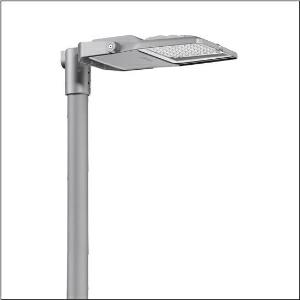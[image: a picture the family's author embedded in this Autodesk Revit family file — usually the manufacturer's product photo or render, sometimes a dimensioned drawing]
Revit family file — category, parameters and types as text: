
# Revit family: floodlight_fl_21_mini___pl33t_5xa7775d2f3a_2fb5
name_source: partatom
category: Lighting Fixtures
units: mm (PartAtom-declared; Revit-internal decimal feet)

## family parameters
Cut with Voids When Loaded = No
Host = Face
Light Source = No
Part Type = Normal
Room Calculation Point = No
Round Connector Dimension = Use Diameter
Shared = No

## types (1)
- --- (1 x LED, 17630 lm, 142.9 W, 3000K)
    Apparent Load = 143 VA
    CIE Flux Codes = 26 75 99 100 100
    Color Rendering = 70
    Color Temperature = 3000K
    Default Elevation = 1800 mm
    Description = Floodlight FL 21 mini, floodlight, primary light control with lens, of PMMA, primary optical cover: protective disc, of toughened safety glass, transparent, light distribution: PL33T, light emission: direct distribution, installation type: surface-mounted, LED, High Power LED, rated luminous flux: 17.630lm, luminous efficacy: 123lm/W, light colour: 730, colour temperature: 3000K, control: flexible luminous flux parameterisation, time-dependent luminous flux control, constant luminous flux control, overheat protection, pre-setting: logarithmic dimming characteristic, with terminal, 6-pole, mains connection: 220..240V, AC, 50/60Hz, start of lifetime: 143W, end of service life: 151W, reduction: 63W, luminaire housing, of diecast aluminium, powder-coated, Siteco® metallic grey (DB 702S), corrosivity category C5 mid according to DIN EN ISO 12944, sealing non-destructively replaceable, please order mast flange separately, mast bracket, of steel, galvanised, powder-coated, Siteco® metallic grey (DB 702S), Smart Interface above, protection rating (complete): IP66, insulation class (complete): insulation class II (safety insulation), certification: CE, ENEC, VDE, protection symbol: D, impact resistance: IK08, permissible operating ambient temperature: -40..+40°C, permissible operating ambient temperature for outdoor applications: -40..+50°C, standard: DIN EN 12944, LABS conformity tested according to VDMA 24364:2018-05, packaging unit: 1 piece

Light Distribution: PL33T
    Height = 70 mm
    Lamp = 1 x LED
    Lamp Light Flux = 17630 lm
    Lamp Power = 142.9 W
    Lamp count = 1
    Length = 485 mm
    Luminous efficacy = 123 lm/W
    Manufacturer = Siteco
    ModVariant = No
    Model = 5XA7775D2F3A
    Number of Poles = 1
    OnlyDefault = Yes
    Power Factor = 1
    Product Name = Floodlight FL 21 mini | PL33T
    Product group = floodlight | pylon annexe
    ProductGroupID = 6200
    Protection Class = Protection class II
    Protection Degree = IP 66
    RLX_Detail_Level = 1
    RLX_Emergency_Light_Flux = 0 lm
    RLX_Emergency_Type = 0
    RLX_Emergency_Type_DB = No
    RlxData = <blob elided: 101173 chars, md5=d7d3eece>
    Socket = socket
    Standby Power = 0 W
    System Light Flux = 17630 lm
    System Power = 143 W
    Type Comments = factory setting: luminous flux: 100 % | dim-lin: 254 | 730 mA
    Type Image = l_1007125.jpg
    URL = http://relux.com
    VarID = @adj_118739
    Voltage = 0 V
    Weight = 0.00 kg
    Width = 337 mm

## geometry (parser evidence)
native form markers: Blend x4, Sweep x12
no freeform markers — native parametric forms only
